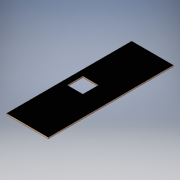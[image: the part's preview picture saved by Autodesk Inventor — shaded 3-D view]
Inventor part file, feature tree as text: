
AUTODESK INVENTOR PART (.ipt)
format: ipt  version: 2016 (Build 200138000, 138)  size: 114,176 bytes
history: native  units: in
note: dims shown in document units (in); Inventor stores cm internally (conversion verified against a paired STEP export)
features: extrude x1, sketch x1
ambient origin geometry x8: Origin, YZ Plane, XZ Plane, XY Plane, X Axis, Y Axis, Z Axis, Center Point
bodies: Solid1 (feature_tree)
feature tree (2):
  extrude  "Extrusion1"  Depth=16.0in
  sketch  "Sketch1"  dims[d0=48.0in d1=16.0in d2=4.0in d3=3.25in d4=3.5in d5=6.0in d6=6.0in d7=0.5in d8=0.0in]
